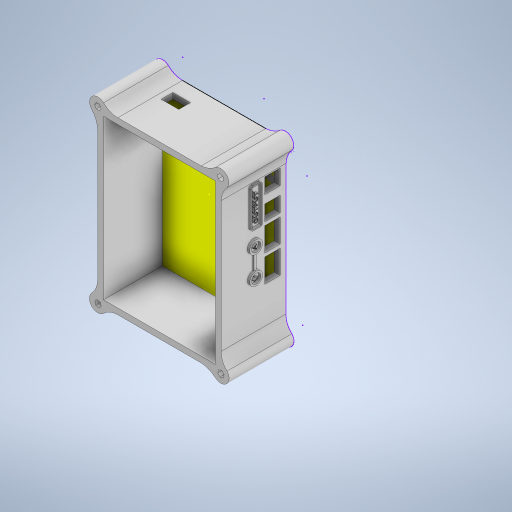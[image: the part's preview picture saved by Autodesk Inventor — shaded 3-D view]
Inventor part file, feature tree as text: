
AUTODESK INVENTOR PART (.ipt)
format: ipt  version: 2024 (Build 280153000, 153)  size: 2,015,232 bytes
history: native  units: mm
features: extrude x25, sketch x7, fillet x5, projected_geometry x4
ambient origin geometry x8: Origin, YZ Plane, XZ Plane, XY Plane, X Axis, Y Axis, Z Axis, Center Point
bodies: Solid3 (feature_tree)
feature tree (41):
  sketch  "Sketch3"  dims[d71=5.0mm d72=0.0mm d73=40.0mm d74=0.0mm]
  extrude  "Extrusion24"  Depth=5.0mm TaperAngle=0.0deg
  sketch  "Sketch11"  dims[d123=0.5mm d126=5.0mm]
  extrude  "Extrusion25"  Depth=0.5mm
  extrude  "Extrusion26"  Depth=5.0mm
  extrude  "Extrusion27"  Depth=5.0mm
  extrude  "Extrusion28"  Depth=0.5mm
  extrude  "Extrusion4"  Depth=1.0mm TaperAngle=0.0deg
  extrude  "Extrusion5"  Depth=1.0mm TaperAngle=0.0deg
  sketch  "Sketch14"  dims[d144=0.5mm d145=0.0mm d146=1.0mm d147=0.0mm]
  extrude  "Extrusion29"  Depth=1.0mm TaperAngle=0.0deg
  extrude  "Extrusion30"  Depth=1.0mm TaperAngle=0.0deg
  extrude  "Extrusion31"  Depth=1.0mm TaperAngle=0.0deg
  extrude  "Extrusion32"  Depth=1.0mm TaperAngle=0.0deg
  extrude  "Extrusion33"  Depth=1.0mm TaperAngle=0.0deg
  extrude  "Extrusion34"  Depth=1.0mm TaperAngle=0.0deg
  sketch  "Sketch15"  dims[d148=1.0mm d149=0.0mm d150=0.5mm d151=0.0mm d152=0.5mm d153=0.0mm d154=1.0mm d155=0.0mm d156=1.5mm d157=0.0mm d158=0.5mm d159=0.0mm d160=1.0mm d161=0.0mm d162=2.0mm d163=0.0mm d164=15.0mm d188=5.0mm d190=62.5mm d191=135.0mm d192=10.0mm d193=10.0mm d195=5.000049mm d196=10.0mm d197=4.999951mm d198=5.000455mm d199=10.000503mm d200=5.0mm d201=10.0mm d202=5.0mm d203=10.0mm d206=18.0mm d207=50.428932mm d208=12.071068mm d209=12.071mm d210=12.071mm d211=12.070504mm d212=12.071128mm d213=7.071082mm d214=7.071mm d216=39.824521mm d217=7.071mm d218=12.071mm d219=10.0mm d220=7.071mm d221=12.071mm d223=13.0mm d224=13.0mm d225=7.0mm d226=13.0mm d227=3.0mm d228=20.0mm d229=3.0mm d230=20.0mm d231=17.0mm d233=5.0mm d234=0.0mm d235=55.0mm d236=0.0mm d237=30.0mm d238=0.0mm d239=13.0mm d240=13.0mm d241=13.0mm d242=13.0mm d243=20.0mm d244=13.0mm d245=20.0mm d246=5.0mm d247=5.0mm d248=5.0mm d249=5.0mm d250=5.5mm d251=0.0mm d252=15.0mm d253=10.0mm d254=13.0mm d255=5.5mm d256=0.0mm d264=2.0mm d265=0.0mm d266=1.0mm d267=0.0mm d268=2.0mm d269=0.0mm d270=1.0mm d271=0.0mm d272=3.0mm d273=0.0mm d274=4.0mm d275=0.0mm d295=1.5mm d296=1.5mm d307=1.0mm d308=2.0mm d309=0.0mm d310=1.0mm d311=0.0mm d312=2.0mm d313=0.1mm d314=0.1mm d315=0.1mm d316=1.0mm d69=0.5mm d70=0.872665mm d75=0.5mm d76=0.872665mm d77=0.5mm d78=0.872665mm d173=0.5mm d174=0.872665mm d175=0.5mm d176=0.872665mm d257=0.5mm d258=0.872665mm d305=0.5mm d306=0.872665mm]
  extrude  "Extrusion35"  Depth=1.0mm
  extrude  "Extrusion36"  Depth=5.0mm
  fillet  "Fillet1"  Radius=62.5mm
  fillet  "Fillet2"  Radius=135.0mm
  fillet  "Fillet3"  Radius=10.0mm
  fillet  "Fillet4"  Radius=10.0mm
  fillet  "Fillet5"  Radius=5.000049mm
  sketch  "Sketch9"  dims[d107=2.0mm d121=0.5mm]
  extrude  "Extrusion13"  Depth=10.0mm
  extrude  "Extrusion14"  Depth=4.999951mm
  extrude  "Extrusion15"  Depth=5.000455mm
  extrude  "Extrusion16"  Depth=10.000503mm
  extrude  "Extrusion17"  Depth=5.0mm
  extrude  "Extrusion18"  Depth=10.0mm
  extrude  "Extrusion19"  Depth=5.0mm
  extrude  "Extrusion20"  Depth=10.0mm
  extrude  "Extrusion21"  Depth=1.0mm
  extrude  "Extrusion22"  Depth=1.0mm
  projected_geometry  "Projected Loop9"
  sketch  "Sketch12"  dims[d127=5.0mm d128=0.5mm]
  projected_geometry  "Projected Loop12"
  sketch  "Sketch13"  dims[d129=0.5mm d130=0.5mm]
  projected_geometry  "Projected Loop13"
  projected_geometry  "Projected Loop14"
